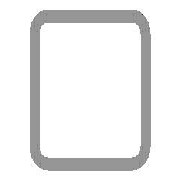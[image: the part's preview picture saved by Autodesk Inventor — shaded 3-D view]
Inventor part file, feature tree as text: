
AUTODESK INVENTOR PART (.ipt)
format: ipt  version: 2025.3 (Build 293356030, 356C)  size: 134,144 bytes
history: native  units: mm (DEFAULTED — no unit token found)
features: other x4, sketch x1, plane x1
ambient origin geometry x8: Origin, YZ Plane, XZ Plane, XY Plane, X Axis, Y Axis, Z Axis, Center Point
bodies: Solid1 (feature_tree), Body (feature_tree)
feature tree (6):
  parser-record x1  (decoder bookkeeping rows leaked as tree rows — omitted from the tree; the rows remain in map.json)
  other  "Driven Length"
  other  "Start Plane"
  other  "End Plane"
  sketch  "Sketch3"  dims[d3=460.0mm d4=0.0mm d7=4.0mm d9=40.0mm d11=40.0mm d12=2.0mm d13=-0.0mm d14=460.0mm d15=20.0mm d16=20.0mm d17=90.0deg d18=460.0mm]
  plane  "Work Plane3"
